# Revit family: HL_RU_Roof drain_HL64.1B-B-221103
name_source: partatom
category: Instalační zařizovací předměty
units: mm (PartAtom-declared; Revit-internal decimal feet)

## family parameters
Bod výpočtu místnosti = Ano
Kóta kulaté spojky = Použít průměr
Nadpis OmniClass = Deck Waste Water Drains
Ořezat dutým tvarem při načtení = Ne
Sdílené = Ne
Typ dílu = Normální
Vždy vertikální = Ano
Založené na pracovní rovině = Ne
Číslo OmniClass = 23.70.50.21.24.14

## types (1)
- HL_Кровельная воронка_HL64.1B
    EAN = 9003076814121
    Indexovaná poznámka = HL64.1B
    Komentáře k typům = HL64.1B Кровельная воронка DN75/110 горизонтальный с зажимным элементом и подогревом (10_30Вт/230В). Проходная _ 148х148мм/137х137мм.,
    Model = HL64.1B
    Popis = Кровельные воронки
    Přípoj CW = Ne
    Přípoj HW = Ne
    Přípoj odpadních dílů = Ano
    Přípoj ventilace = Ne
    URL = http://www.hutterer-lechner.com
    Výchozí výška = 0 mm  [stored 0 ft]
    Výrobce = HL Hutterer & Lechner GmbH
    ВЕС = 2,04 [kg]
    ВЫСОТА МОНТАЖА = 167 mm
    МАКСИМАЛЬНАЯ НАГРУЗКА КЛАССА = K - 300 kg
    МАТЕРИАЛ = PP
    НАСАДКА = 12-65mm/148x148mm
    ПРОИЗВОДИТЕЛЬНОСТЬ = 3,7 l/s
    РАЗМЕР = DN75/110
    РЕШЁТКА = Edelstahl 137x137mm

note: [stored X ft] marks values corroborated as IEEE doubles in the binary element streams (Revit-internal decimal feet)

## geometry (parser evidence)
native form markers: Sweep x17
no freeform markers — native parametric forms only
